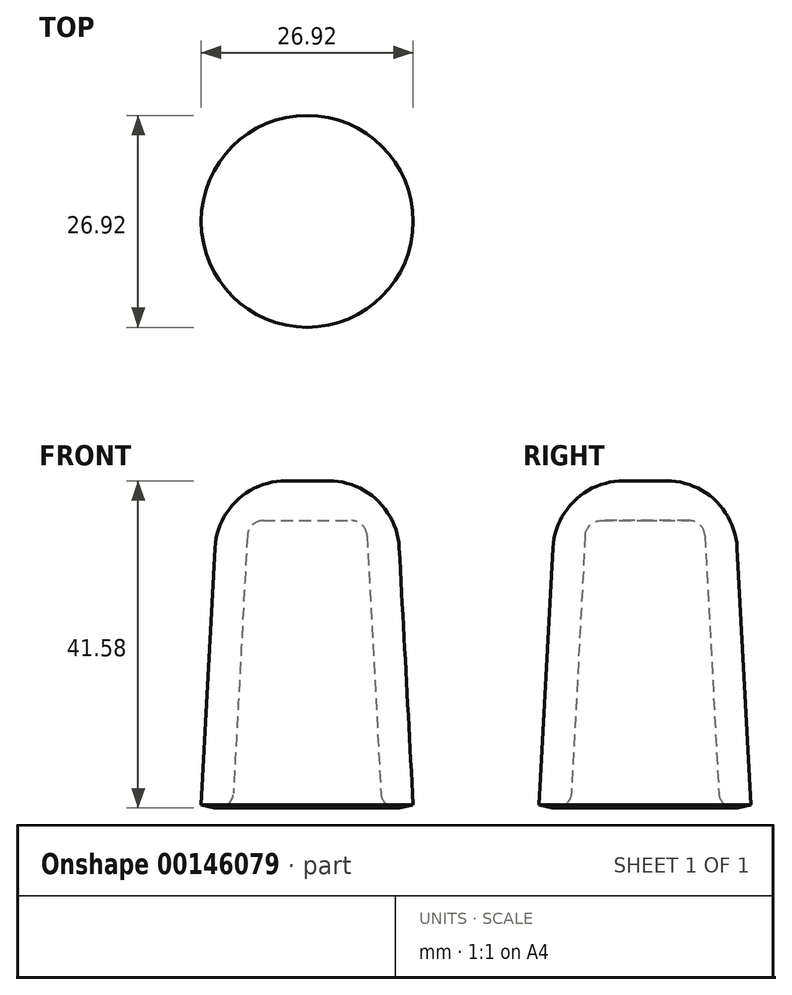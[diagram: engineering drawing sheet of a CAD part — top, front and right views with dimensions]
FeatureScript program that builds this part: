
annotation { "Feature Type Name" : "Feature", "Feature Type Description" : "" }
export const myFeature = defineFeature(function(context is Context, id is Id, definition is map)
    precondition{}
    {
        {
            var Q0;
            Q0=qCreatedBy(makeId("Front.planeOp"),FACE);
            var sketch = newSketch(context, id + "F0", { "sketchPlane" : qUnion([Q0])});
            skLineSegment(sketch, "E0", {"start": v(-7.5, 23.76) * mm, "end": v(-9.5, -13.24) * mm});
            skLineSegment(sketch, "E1", {"start": v(0, 37.05) * mm, "end": v(0, -30.43) * mm, "construction": true});
            skLineSegment(sketch, "E2.0", {"start": v(-11.5, 23.79) * mm, "end": v(-13.46, -12.33) * mm});
            skLineSegment(sketch, "E3", {"start": v(-13.46, -12.33) * mm, "end": v(-9.5, -13.24) * mm});
            skLineSegment(sketch, "E4", {"start": v(-13.46, -12.33) * mm, "end": v(-11.5, 23.79) * mm});
            skLineSegment(sketch, "E5", {"start": v(-9.5, -13.24) * mm, "end": v(-13.46, -12.33) * mm});
            skLineSegment(sketch, "E6", {"start": v(-7.5, 23.76) * mm, "end": v(0, 23.76) * mm});
            skLineSegment(sketch, "E7", {"start": v(0, 23.76) * mm, "end": v(0, 28.82) * mm});
            skLineSegment(sketch, "E8", {"start": v(0, 28.82) * mm, "end": v(-11.5, 28.82) * mm});
            skLineSegment(sketch, "E9", {"start": v(-11.5, 28.82) * mm, "end": v(-11.5, 23.79) * mm});
            skSolve(sketch);
        }
        {
            var Q0;
            {var subQ8=sQuery(id+"F0.wireOp",EDGE,"E0");Q0=makeQuery(id+"F0.imprint","IMPRINT",FACE,{"disambiguationData":[TD([[makeQuery(id+"F0.imprint","IMPRINT",EDGE,{"derivedFrom":subQ8}),-1.0]])]});}
            var Q1;
            Q1=sQuery(id+"F0.wireOp",EDGE,"E1");
            revolve(context, id + "F1", {"entities" : qUnion([Q0]), "axis" : qUnion([Q1]), "revolveType" : RevolveType.FULL});
        }
        {
            var Q0;
            Q0=makeQuery(id+"F1.opRevolve","SWEPT_EDGE",EDGE,{"disambiguationData":[OSD([sQuery(id+"F0.wireOp",EDGE,"E0"),sQuery(id+"F0.wireOp",EDGE,"E5")])]});
            var Q1;
            Q1=makeQuery(id+"F1.opRevolve","SWEPT_EDGE",EDGE,{"disambiguationData":[OSD([sQuery(id+"F0.wireOp",EDGE,"E4"),sQuery(id+"F0.wireOp",EDGE,"E5")])]});
            fillet(context, id + "F2", {"entities" : qUnion([Q0, Q1]), "radius" : 2 * mm, "tangentPropagation" : true, "allowEdgeOverflow" : false});
        }
        {
            var Q0;
            Q0=makeQuery(id+"F1.opRevolve","SWEPT_EDGE",EDGE,{"disambiguationData":[OSD([sQuery(id+"F0.wireOp",EDGE,"E8"),sQuery(id+"F0.wireOp",EDGE,"E9")])]});
            fillet(context, id + "F3", {"entities" : qUnion([Q0]), "radius" : 9 * mm, "tangentPropagation" : true, "allowEdgeOverflow" : false});
        }
    });
